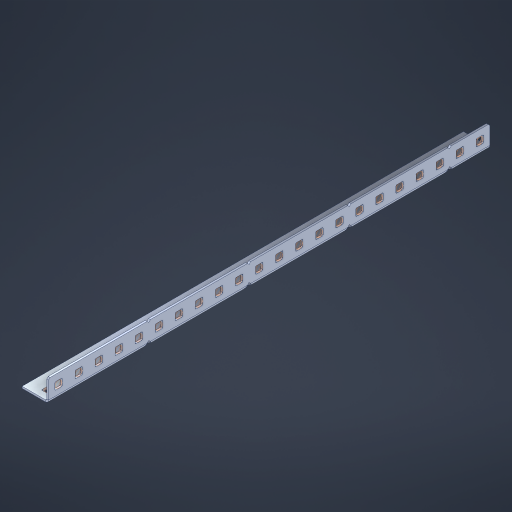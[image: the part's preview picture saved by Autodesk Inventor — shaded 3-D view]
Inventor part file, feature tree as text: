
AUTODESK INVENTOR PART (.ipt)
format: ipt  version: 2023 (Build 270158000, 158)  size: 793,600 bytes
history: native  units: in
note: dims shown in document units (in); Inventor stores cm internally (conversion verified against a paired STEP export)
features: other x49, extrude x43, sheet_metal_op x10, sketch x8, mirror x1, pattern_linear x1, chamfer x1
ambient origin geometry x8: Origin, YZ Plane, XZ Plane, XY Plane, X Axis, Y Axis, Z Axis, Center Point
bodies: Solid1 (feature_tree), Body (feature_tree)
feature tree (113):
  other  "Flange Pattern Plane"
  sheet_metal_op  "Flange Pattern"
  sheet_metal_op  "Body Pattern"
  other  "Arc Length"
  mirror  "Notch Mirror"
  pattern_linear  "Notch Pattern"  Spacing1=0.1875in  [1 undecoded]
  chamfer  "End Chamfer"
  extrude  "Half Cut"  Depth=0.0469in
  sketch  "Sketch1"  dims[d0=2.5in]
  other  "Plate1"
  sketch  "Sketch2"  dims[d1=11.0in]
  other  "Plate2"
  sheet_metal_op  "Bend1"
  sheet_metal_op  "Corner1"
  sketch  "Sketch3"  dims[d2=0.0469in]
  other  "Flange Pattern Sketch"
  sketch  "Sketch7"  dims[d3=0.0469in]
  other  "Srf1"
  other  "Srf2"
  sketch  "Sketch8"  dims[d4=0.0234in]
  sketch  "Sketch9"  dims[d5=0.0938in]
  other  "Srf91"
  sheet_metal_op  "Body Pattern Sketch"
  other  "Srf92"
  sketch  "Sketch13"  dims[d6=0.0469in]
  sketch  "Sketch14"  dims[d7=0.5in d8=90.0deg d9=0.0312in d10=0.1875in d11=0.0469in d12=0.0469in d16=0.182in d17=0.02in d18=0.0469in d19=0.0in d20=0.25in d21=0.25in d46=0.172in d47=1.0in d48=0.0in d49=0.182in d50=0.02in d51=0.25in d52=0.25in d53=0.0469in d54=0.0in d55=0.172in d56=1.0in d57=0.0in d60=8.6614in d62=0.5in d63=0.3937in d65=0.5in d85=0.1227in d86=0.1659in d88=0.04in d89=0.0469in d90=0.0in d91=0.04in d92=0.0491in d95=2.5in d96=0.04in d97=0.25in d98=45.0deg d101=0.0in d102=2.497in d131=0.5in d132=8.6614in d134=0.5in d139=0.5in]
  other  "Srf856"
  other  "Srf1310"
  other  "Srf1311"
  other  "Srf1312"
  other  "Srf1376"
  other  "Srf1377"
  other  "Srf1728"
  other  "Srf1755"
  other  "Srf1878"
  other  "Srf1879"
  other  "Srf1880"
  other  "Srf1881"
  other  "Srf1882"
  other  "Srf1883"
  other  "Srf1884"
  other  "Srf1885"
  other  "Srf1886"
  other  "Srf1887"
  other  "Srf1888"
  other  "Srf1889"
  other  "Srf1890"
  other  "Srf1891"
  other  "Srf1892"
  other  "Srf1893"
  other  "Srf1942"
  other  "Srf1943"
  other  "Srf1944"
  other  "Srf1945"
  other  "Srf1946"
  other  "Srf1947"
  other  "Srf1948"
  other  "Srf1949"
  other  "Srf1950"
  other  "Srf1951"
  other  "Srf1952"
  other  "Srf1953"
  other  "Srf1954"
  other  "Srf1955"
  other  "Srf1956"
  other  "Srf1957"
  sheet_metal_op  "Flange Stamp"
  sheet_metal_op  "Flange Circle"
  sheet_metal_op  "Body Stamp"
  sheet_metal_op  "Body Circle"
  sheet_metal_op  "Notch"
  extrude  "ExtrusionSrf2"  Depth=0.0469in
  extrude  "ExtrusionSrf92"  Depth=0.5in
  extrude  "ExtrusionSrf856"  Depth=0.02in
  extrude  "ExtrusionSrf1310"  Depth=0.0469in
  extrude  "ExtrusionSrf1311"  TaperAngle=0.0deg  [1 undecoded]
  extrude  "ExtrusionSrf1312"  Depth=0.5in
  extrude  "ExtrusionSrf1376"  Depth=0.5in
  extrude  "ExtrusionSrf1377"  Depth=0.5in
  extrude  "ExtrusionSrf1728"  Depth=0.5in TaperAngle=0.0deg
  extrude  "ExtrusionSrf1755"  Depth=0.5in
  extrude  "ExtrusionSrf1878"  Depth=0.02in
  extrude  "ExtrusionSrf1879"  Depth=0.5in
  extrude  "ExtrusionSrf1880"  Depth=0.5in
  extrude  "ExtrusionSrf1881"  Depth=0.0469in
  extrude  "ExtrusionSrf1882"  TaperAngle=0.0deg  [1 undecoded]
  extrude  "ExtrusionSrf1883"  Depth=0.5in
  extrude  "ExtrusionSrf1884"  Depth=0.5in TaperAngle=0.0deg
  extrude  "ExtrusionSrf1885"  Depth=0.5in
  extrude  "ExtrusionSrf1886"  Depth=0.5in
  extrude  "ExtrusionSrf1887"  Depth=0.5in
  extrude  "ExtrusionSrf1888"  Depth=0.5in
  extrude  "ExtrusionSrf1889"  Depth=0.5in
  extrude  "ExtrusionSrf1890"  Depth=0.0469in
  extrude  "ExtrusionSrf1891"  TaperAngle=0.0deg  [1 undecoded]
  extrude  "ExtrusionSrf1892"  Depth=0.5in
  extrude  "ExtrusionSrf1893"  Depth=0.5in
  extrude  "ExtrusionSrf1942"  Depth=0.5in
  extrude  "ExtrusionSrf1943"  Depth=0.5in TaperAngle=45.0deg
  extrude  "ExtrusionSrf1944"  TaperAngle=0.0deg  [1 undecoded]
  extrude  "ExtrusionSrf1945"  Depth=0.5in
  extrude  "ExtrusionSrf1946"  Depth=0.5in
  extrude  "ExtrusionSrf1947"  Depth=0.5in
  extrude  "ExtrusionSrf1948"  Depth=0.5in
  extrude  "ExtrusionSrf1949"  Depth=0.5in
  extrude  "ExtrusionSrf1950"  [1 undecoded]
  extrude  "ExtrusionSrf1951"  [1 undecoded]
  extrude  "ExtrusionSrf1952"  [1 undecoded]
  extrude  "ExtrusionSrf1953"  [1 undecoded]
  extrude  "ExtrusionSrf1954"  [1 undecoded]
  extrude  "ExtrusionSrf1955"  [1 undecoded]
  extrude  "ExtrusionSrf1956"  [1 undecoded]
  extrude  "ExtrusionSrf1957"  [1 undecoded]
note: 13 required parameter values undecoded (feature->parameter linkage not recoverable at this tier; creation-order binding heuristic only, values carry confidence <= 0.55)
